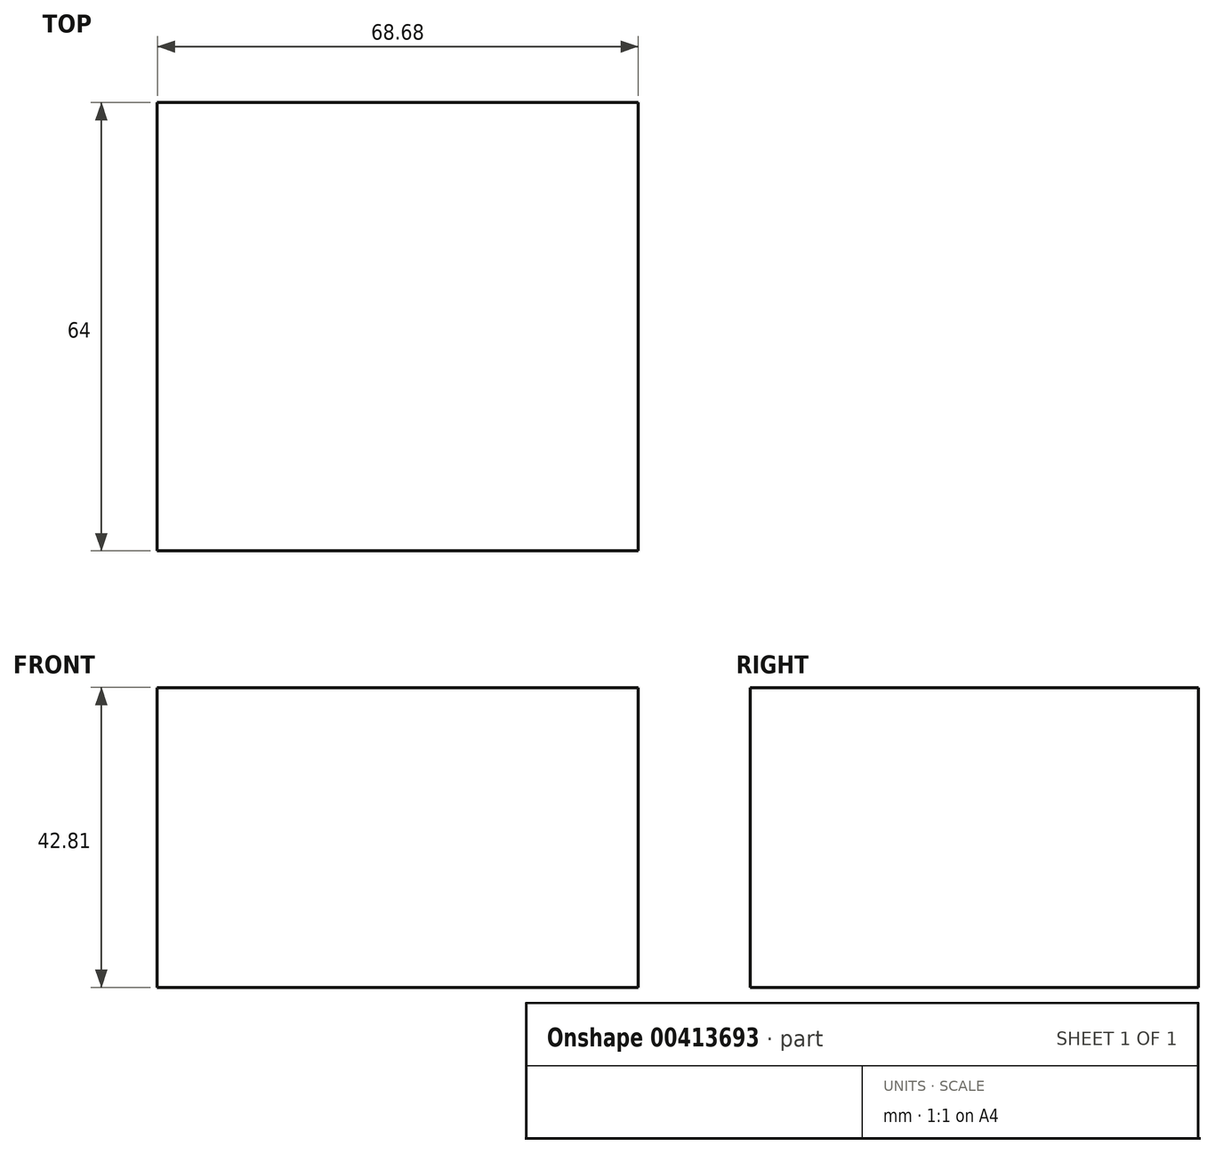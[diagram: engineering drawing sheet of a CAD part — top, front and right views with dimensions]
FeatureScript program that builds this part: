
annotation { "Feature Type Name" : "Feature", "Feature Type Description" : "" }
export const myFeature = defineFeature(function(context is Context, id is Id, definition is map)
    precondition{}
    {
        {
            var Q0;
            Q0=qCreatedBy(makeId("Front.planeOp"),FACE);
            var sketch = newSketch(context, id + "F0", { "sketchPlane" : qUnion([Q0])});
            skLineSegment(sketch, "E0.bottom", {"start": v(-34.18, 20.93) * mm, "end": v(34.5, 20.93) * mm});
            skLineSegment(sketch, "E0.top", {"start": v(-34.18, -21.88) * mm, "end": v(34.5, -21.88) * mm});
            skLineSegment(sketch, "E0.left", {"start": v(-34.18, 20.93) * mm, "end": v(-34.18, -21.88) * mm});
            skLineSegment(sketch, "E0.right", {"start": v(34.5, 20.93) * mm, "end": v(34.5, -21.88) * mm});
            skSolve(sketch);
        }
        {
            var Q0;
            Q0 = qSketchRegion(id + "F0", true);
            extrude(context, id + "F1", {"entities" : qUnion([Q0]), "depth" : 64 * mm, "offsetDistance" : 25 * mm, "symmetric" : true});
        }
    });
